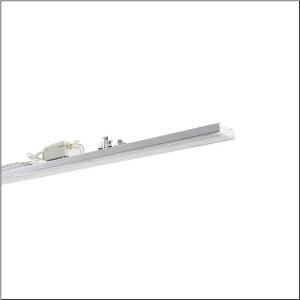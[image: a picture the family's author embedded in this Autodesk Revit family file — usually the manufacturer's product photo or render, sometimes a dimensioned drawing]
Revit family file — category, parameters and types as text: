
# Revit family: licross_r__21_recessed_mo_52tl11cn49xg_87da
name_source: partatom
category: Lighting Fixtures
units: mm (PartAtom-declared; Revit-internal decimal feet)

## family parameters
Cut with Voids When Loaded = No
Host = Face
Light Source = No
Part Type = Normal
Room Calculation Point = No
Round Connector Dimension = Use Diameter
Shared = No

## types (1)
- --- (1 x LED, 9120 lm, 49.9 W, 4000K)
    Apparent Load = 50 VA
    CIE Flux Codes = 89 96 99 100 100
    Color Rendering = 80
    Color Temperature = 4000K
    Default Elevation = 1800 mm
    Description = Licross® 21 Recessed MO, luminaire insert, of sheet steel, galvanised, coil coated, white, length: 1.500mm, width: 66mm, height: 67mm, LED rated luminous flux: 9.120lm, light colour: 840, control gear: ON/OFF Multilumen, CLOi, control gear: ECG Multilumen, with plug, 3-pole, with phase selection, mains connection: 220..240V, AC, 50/60Hz, start of lifetime: 50W, end of service life: 61W, halogen-free wiring, primary light control with lens, of plastic, primary optical cover: cover, of PMMA, light emission: direct distribution, primary light characteristic: symmetric, protection rating (complete): IP40, insulation class (complete): insulation class I (protective earthing), certification: CE, ENEC, VDE, UKCA, protection symbol: D if used in an environment without relevant dust loads with corresponding accessories, impact resistance: IK06, permissible ambient temperature for indoor applications: -35..+40°C, corresponds to IFS (International Featured Standards) requirements for safety and quality in the food industry, reducing of maximum allowable ambient temperature of 5°C with ceiling mounting, LABS conformity tested according to VDMA 24364:2018-05, packaging unit: 1 piece
    Height = 58 mm
    Lamp = 1 x LED
    Lamp Light Flux = 9120 lm
    Lamp Power = 49.9 W
    Lamp count = 1
    Length = 1500 mm
    Luminous efficacy = 183 lm/W
    Manufacturer = Siteco
    ModVariant = No
    Model = 52TL11CN49XG
    Mounting Place = Ceiling
    Mounting Type = Pendant
    Number of Poles = 1
    OnlyDefault = Yes
    Power Factor = 1
    Product Name = Licross® 21 Recessed MO
    Product group = luminaire insert
    ProductGroupID = 901
    Protection Class = Protection class I
    Protection Degree = IP 40
    RLX_Detail_Level = 1
    RLX_Emergency_Light_Flux = 0 lm
    RLX_Emergency_Type = 0
    RLX_Emergency_Type_DB = No
    RlxData = <blob elided: 22297 chars, md5=74c82fa2>
    Socket = socket
    Standby Power = 0 W
    System Light Flux = 9120 lm
    System Power = 50 W
    Type Comments = factory setting: luminous flux: 100 % | (A | C | E) | 116 mA
    Type Image = l_1296930.jpg
    URL = http://relux.com
    VarID = @adj_040769
    Voltage = 0 V
    Weight = 0.00 kg
    Width = 66 mm

## geometry (parser evidence)
native form markers: Blend x4, Sweep x12
no freeform markers — native parametric forms only
